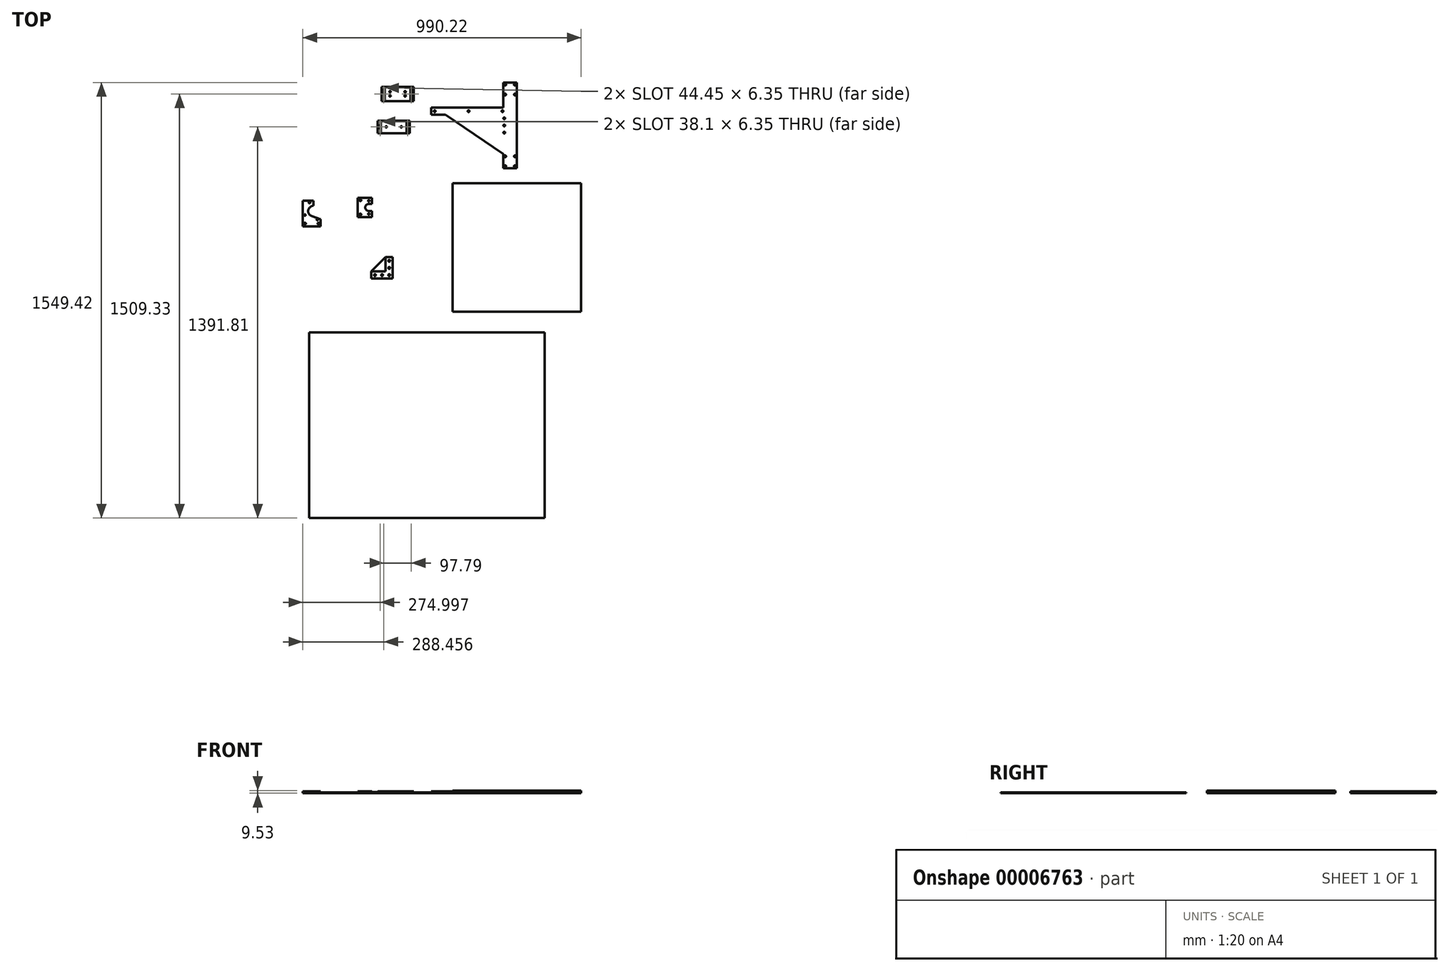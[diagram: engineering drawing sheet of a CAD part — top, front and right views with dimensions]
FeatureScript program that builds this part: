
annotation { "Feature Type Name" : "Feature", "Feature Type Description" : "" }
export const myFeature = defineFeature(function(context is Context, id is Id, definition is map)
    precondition{}
    {
        {
            var Q0;
            Q0=qCreatedBy(makeId("Top.planeOp"),FACE);
            var sketch = newSketch(context, id + "F0", { "sketchPlane" : qUnion([Q0])});
            skLineSegment(sketch, "E0.rect.bottom", {"start": v(228.6, 228.6) * mm, "end": v(-228.6, 228.6) * mm});
            skLineSegment(sketch, "E0.rect.top", {"start": v(228.6, -228.6) * mm, "end": v(-228.6, -228.6) * mm});
            skLineSegment(sketch, "E0.rect.left", {"start": v(228.6, 228.6) * mm, "end": v(228.6, -228.6) * mm});
            skLineSegment(sketch, "E0.rect.right", {"start": v(-228.6, 228.6) * mm, "end": v(-228.6, -228.6) * mm});
            skPoint(sketch, "E0.rect.middle", {"position": v(0, 0) * mm});
            skSolve(sketch);
        }
        {
            var Q0;
            Q0=makeQuery(id+"F0.imprint","IMPRINT",FACE,{"disambiguationData":[TD([[makeQuery(id+"F0.imprint","IMPRINT",EDGE,{"derivedFrom":sQuery(id+"F0.wireOp",EDGE,"E0.rect.bottom")}),1.0]])]});
            extrude(context, id + "F1", {"entities" : qUnion([Q0]), "depth" : 9.52 * mm});
        }
        {
            var Q0;
            Q0=qCreatedBy(makeId("Top.planeOp"),FACE);
            var sketch = newSketch(context, id + "F2", { "sketchPlane" : qUnion([Q0])});
            skLineSegment(sketch, "E1.rect.left", {"start": v(0, 281.9) * mm, "end": v(0, 586.7) * mm});
            skLineSegment(sketch, "E2", {"start": v(-47.75, 281.9) * mm, "end": v(0, 281.9) * mm});
            skLineSegment(sketch, "E3", {"start": v(-47.75, 586.7) * mm, "end": v(0, 586.7) * mm});
            skLineSegment(sketch, "E4", {"start": v(-304.8, 497.8) * mm, "end": v(-304.8, 472.4) * mm});
            skLineSegment(sketch, "E5", {"start": v(-47.75, 281.9) * mm, "end": v(-47.75, 332.7) * mm});
            skLineSegment(sketch, "E6", {"start": v(-47.75, 586.7) * mm, "end": v(-47.75, 497.8) * mm});
            skLineSegment(sketch, "E7", {"start": v(-304.8, 497.8) * mm, "end": v(-254, 497.8) * mm});
            skLineSegment(sketch, "E8", {"start": v(-254, 497.8) * mm, "end": v(-47.75, 497.8) * mm});
            skLineSegment(sketch, "E9", {"start": v(-304.8, 472.4) * mm, "end": v(-254, 472.4) * mm});
            skLineSegment(sketch, "E10", {"start": v(-254, 472.4) * mm, "end": v(-47.75, 332.7) * mm});
            skLineSegment(sketch, "E11", {"start": v(-304.8, 485.1) * mm, "end": v(0, 485.1) * mm, "construction": true});
            skLineSegment(sketch, "E12", {"start": v(-41.38, 586.7) * mm, "end": v(-41.38, 579.19) * mm, "construction": true});
            skLineSegment(sketch, "E13", {"start": v(-6.38, 586.7) * mm, "end": v(-6.38, 281.9) * mm, "construction": true});
            skLineSegment(sketch, "E14", {"start": v(-47.75, 579.19) * mm, "end": v(0, 579.19) * mm, "construction": true});
            skLineSegment(sketch, "E15", {"start": v(-47.75, 544.19) * mm, "end": v(0, 544.19) * mm, "construction": true});
            skLineSegment(sketch, "E16", {"start": v(-47.75, 324.43) * mm, "end": v(0, 324.43) * mm, "construction": true});
            skLineSegment(sketch, "E17", {"start": v(-47.75, 289.43) * mm, "end": v(-41.38, 289.43) * mm, "construction": true});
            skLineSegment(sketch, "E18", {"start": v(-41.38, 324.43) * mm, "end": v(-41.38, 289.43) * mm, "construction": true});
            skLineSegment(sketch, "E19", {"start": v(-41.38, 289.43) * mm, "end": v(-41.38, 281.9) * mm, "construction": true});
            skLineSegment(sketch, "E20", {"start": v(-41.38, 289.43) * mm, "end": v(-6.38, 289.43) * mm, "construction": true});
            skLineSegment(sketch, "E21", {"start": v(-6.38, 289.43) * mm, "end": v(0, 289.43) * mm, "construction": true});
            skLineSegment(sketch, "E22", {"start": v(-41.38, 579.19) * mm, "end": v(-41.38, 544.19) * mm, "construction": true});
            skLineSegment(sketch, "E23", {"start": v(-41.38, 544.19) * mm, "end": v(-41.38, 324.43) * mm, "construction": true});
            skPoint(sketch, "E24", {"position": v(-41.38, 306.93) * mm});
            skPoint(sketch, "E25", {"position": v(-41.38, 561.69) * mm});
            skCircle(sketch, "E26", {"center": v(-41.38, 324.43) * mm, "radius": 3.2 * mm});
            skCircle(sketch, "E27", {"center": v(-6.38, 324.43) * mm, "radius": 3.2 * mm});
            skCircle(sketch, "E28", {"center": v(-41.38, 289.43) * mm, "radius": 3.2 * mm});
            skCircle(sketch, "E29", {"center": v(-6.38, 289.43) * mm, "radius": 3.2 * mm});
            skCircle(sketch, "E30", {"center": v(-41.38, 579.19) * mm, "radius": 3.2 * mm});
            skCircle(sketch, "E31", {"center": v(-6.38, 579.19) * mm, "radius": 3.2 * mm});
            skCircle(sketch, "E32", {"center": v(-41.38, 544.19) * mm, "radius": 3.2 * mm});
            skCircle(sketch, "E33", {"center": v(-6.38, 544.19) * mm, "radius": 3.2 * mm});
            skCircle(sketch, "E34", {"center": v(-171.45, 485.1) * mm, "radius": 3.17 * mm});
            skCircle(sketch, "E35", {"center": v(-50.8, 485.1) * mm, "radius": 3.17 * mm});
            skCircle(sketch, "E36", {"center": v(-292.1, 485.1) * mm, "radius": 3.17 * mm});
            skCircle(sketch, "E37", {"center": v(-69.85, 459.7) * mm, "radius": 2.55 * mm, "construction": true});
            skCircle(sketch, "E38", {"center": v(-69.85, 434.3) * mm, "radius": 2.55 * mm, "construction": true});
            skCircle(sketch, "E39", {"center": v(-95.25, 459.7) * mm, "radius": 2.55 * mm, "construction": true});
            skCircle(sketch, "E40", {"center": v(-95.25, 434.3) * mm, "radius": 2.55 * mm, "construction": true});
            skLineSegment(sketch, "E41", {"start": v(-44.45, 608.23) * mm, "end": v(-44.45, 265.2) * mm, "construction": true});
            skCircle(sketch, "E42", {"center": v(-44.45, 459.7) * mm, "radius": 3.17 * mm});
            skCircle(sketch, "E43", {"center": v(-44.45, 434.3) * mm, "radius": 3.17 * mm});
            skCircle(sketch, "E44", {"center": v(-44.45, 408.9) * mm, "radius": 3.18 * mm});
            skSolve(sketch);
        }
        {
            var Q0;
            Q0=makeQuery(id+"F2.imprint","IMPRINT",FACE,{"disambiguationData":[TD([[makeQuery(id+"F2.imprint","IMPRINT",EDGE,{"derivedFrom":sQuery(id+"F2.wireOp",EDGE,"E1.rect.left")}),1.0]])]});
            extrude(context, id + "F3", {"entities" : qUnion([Q0]), "depth" : 6.35 * mm});
        }
        {
            var Q0;
            Q0=qCreatedBy(makeId("Top.planeOp"),FACE);
            var sketch = newSketch(context, id + "F4", { "sketchPlane" : qUnion([Q0])});
            skLineSegment(sketch, "E45", {"start": v(-517.53, -110.74) * mm, "end": v(-441.33, -110.74) * mm});
            skLineSegment(sketch, "E46", {"start": v(-441.33, -110.74) * mm, "end": v(-441.33, -34.54) * mm});
            skLineSegment(sketch, "E47", {"start": v(-441.33, -34.54) * mm, "end": v(-466.73, -34.54) * mm});
            skLineSegment(sketch, "E48", {"start": v(-466.73, -34.54) * mm, "end": v(-466.73, -85.34) * mm});
            skLineSegment(sketch, "E49", {"start": v(-466.73, -85.34) * mm, "end": v(-517.53, -85.34) * mm});
            skLineSegment(sketch, "E50", {"start": v(-517.53, -85.34) * mm, "end": v(-517.53, -110.74) * mm});
            skCircle(sketch, "E51", {"center": v(-454.03, -98.04) * mm, "radius": 3.26 * mm});
            skCircle(sketch, "E52.1.0.0", {"center": v(-454.03, -72.64) * mm, "radius": 3.26 * mm});
            skCircle(sketch, "E52.2.0.0", {"center": v(-454.03, -47.24) * mm, "radius": 3.26 * mm});
            skLineSegment(sketch, "E52.direction1", {"start": v(-454.03, -98.04) * mm, "end": v(-454.03, -72.64) * mm, "construction": true});
            skCircle(sketch, "E53.1.0.0", {"center": v(-479.43, -98.04) * mm, "radius": 3.26 * mm});
            skCircle(sketch, "E53.2.0.0", {"center": v(-504.83, -98.04) * mm, "radius": 3.26 * mm});
            skLineSegment(sketch, "E53.direction1", {"start": v(-454.03, -98.04) * mm, "end": v(-479.43, -98.04) * mm, "construction": true});
            skLineSegment(sketch, "E54", {"start": v(-517.53, -85.34) * mm, "end": v(-466.73, -34.54) * mm});
            skSolve(sketch);
        }
        {
            var Q0;
            Q0=makeQuery(id+"F4.imprint","IMPRINT",FACE,{"disambiguationData":[TD([[makeQuery(id+"F4.imprint","IMPRINT",EDGE,{"derivedFrom":sQuery(id+"F4.wireOp",EDGE,"E45")}),1.0]])]});
            extrude(context, id + "F5", {"entities" : qUnion([Q0]), "depth" : 4.78 * mm});
        }
        {
            var Q0;
            Q0=makeQuery(id+"F4.imprint","IMPRINT",FACE,{"disambiguationData":[TD([[makeQuery(id+"F4.imprint","IMPRINT",EDGE,{"derivedFrom":sQuery(id+"F4.wireOp",EDGE,"E48")}),-1.0]])]});
            var Q1;
            Q1=makeQuery(id+"F4.imprint","IMPRINT",FACE,{"disambiguationData":[TD([[makeQuery(id+"F4.imprint","IMPRINT",EDGE,{"derivedFrom":sQuery(id+"F4.wireOp",EDGE,"E45")}),1.0]])]});
            extrude(context, id + "F6", {"entities" : qUnion([Q0, Q1]), "depth" : 4.78 * mm});
        }
        {
            var Q0;
            Q0=qCreatedBy(makeId("Top.planeOp"),FACE);
            var sketch = newSketch(context, id + "F7", { "sketchPlane" : qUnion([Q0])});
            skLineSegment(sketch, "E55.bottom", {"start": v(-566.8, 176.8) * mm, "end": v(-526.52, 176.8) * mm});
            skLineSegment(sketch, "E55.top", {"start": v(-566.8, 108.21) * mm, "end": v(-526.52, 108.21) * mm});
            skLineSegment(sketch, "E55.left", {"start": v(-566.8, 176.8) * mm, "end": v(-566.8, 108.21) * mm});
            skLineSegment(sketch, "E55.right", {"start": v(-526.52, 176.8) * mm, "end": v(-526.52, 155.2) * mm, "construction": true});
            skArc(sketch, "E56", {"start": v(-526.52, 155.2) * mm, "mid": v(-539.22, 142.5) * mm, "end": v(-526.52, 129.8) * mm});
            skLineSegment(sketch, "E57.trimOffspring", {"start": v(-526.52, 129.8) * mm, "end": v(-526.52, 108.21) * mm, "construction": true});
            skLineSegment(sketch, "E58", {"start": v(-526.52, 108.21) * mm, "end": v(-516, 108.21) * mm});
            skLineSegment(sketch, "E59", {"start": v(-516, 108.21) * mm, "end": v(-516, 129.8) * mm});
            skLineSegment(sketch, "E60", {"start": v(-516, 129.8) * mm, "end": v(-526.52, 129.8) * mm});
            skLineSegment(sketch, "E61", {"start": v(-526.52, 155.2) * mm, "end": v(-516, 155.2) * mm});
            skLineSegment(sketch, "E62", {"start": v(-516, 155.2) * mm, "end": v(-516, 176.8) * mm});
            skLineSegment(sketch, "E63", {"start": v(-516, 176.8) * mm, "end": v(-526.52, 176.8) * mm});
            skCircle(sketch, "E64", {"center": v(-526.52, 166) * mm, "radius": 2.55 * mm});
            skCircle(sketch, "E65", {"center": v(-526.52, 119) * mm, "radius": 2.55 * mm});
            skCircle(sketch, "E66", {"center": v(-556.64, 167.9) * mm, "radius": 3.18 * mm});
            skCircle(sketch, "E67", {"center": v(-556.64, 117.1) * mm, "radius": 3.18 * mm});
            skSolve(sketch);
        }
        {
            var Q0;
            Q0=makeQuery(id+"F7.imprint","IMPRINT",FACE,{"disambiguationData":[TD([[makeQuery(id+"F7.imprint","IMPRINT",EDGE,{"derivedFrom":sQuery(id+"F7.wireOp",EDGE,"E55.bottom")}),-1.0]])]});
            extrude(context, id + "F8", {"entities" : qUnion([Q0]), "depth" : 6.35 * mm});
        }
        {
            var Q0;
            Q0=qCreatedBy(makeId("Top.planeOp"),FACE);
            var sketch = newSketch(context, id + "F9", { "sketchPlane" : qUnion([Q0])});
            skLineSegment(sketch, "E68.rect.bottom", {"start": v(99.07, -962.71) * mm, "end": v(-739.13, -962.71) * mm});
            skLineSegment(sketch, "E68.rect.top", {"start": v(99.07, -302.31) * mm, "end": v(-739.13, -302.31) * mm});
            skLineSegment(sketch, "E68.rect.left", {"start": v(99.07, -962.71) * mm, "end": v(99.07, -302.31) * mm});
            skLineSegment(sketch, "E68.rect.right", {"start": v(-739.13, -962.71) * mm, "end": v(-739.13, -302.31) * mm});
            skPoint(sketch, "E68.rect.middle", {"position": v(-320.03, -632.51) * mm});
            skSolve(sketch);
        }
        {
            var Q0;
            Q0=makeQuery(id+"F9.imprint","IMPRINT",FACE,{"disambiguationData":[TD([[makeQuery(id+"F9.imprint","IMPRINT",EDGE,{"derivedFrom":sQuery(id+"F9.wireOp",EDGE,"E68.rect.bottom")}),-1.0]])]});
            extrude(context, id + "F10", {"entities" : qUnion([Q0]), "depth" : 3.17 * mm});
        }
        {
            var Q0;
            Q0=makeQuery(id+"F1.opExtrude","CAP_FACE",FACE,{"disambiguationData":[OSD([sQuery(id+"F0.wireOp",EDGE,"E0.rect.bottom"),sQuery(id+"F0.wireOp",EDGE,"E0.rect.top"),sQuery(id+"F0.wireOp",EDGE,"E0.rect.left"),sQuery(id+"F0.wireOp",EDGE,"E0.rect.right")])],"isStart":true});
            var sketch = newSketch(context, id + "F11", { "sketchPlane" : qUnion([Q0])});
            skLineSegment(sketch, "E69", {"start": v(0, 177.8) * mm, "end": v(152.4, 177.8) * mm, "construction": true});
            skLineSegment(sketch, "E70", {"start": v(76.2, 59.27) * mm, "end": v(-76.2, 59.27) * mm, "construction": true});
            skLineSegment(sketch, "E71", {"start": v(-152.4, -59.27) * mm, "end": v(152.4, -59.27) * mm, "construction": true});
            skLineSegment(sketch, "E72", {"start": v(76.2, -177.8) * mm, "end": v(-76.2, -177.8) * mm, "construction": true});
            skLineSegment(sketch, "E73", {"start": v(76.2, -177.8) * mm, "end": v(76.2, -59.27) * mm, "construction": true});
            skLineSegment(sketch, "E74", {"start": v(76.2, -59.27) * mm, "end": v(76.2, 59.27) * mm, "construction": true});
            skLineSegment(sketch, "E75", {"start": v(76.2, 59.27) * mm, "end": v(76.2, 177.8) * mm, "construction": true});
            skPoint(sketch, "E76", {"position": v(0, 177.8) * mm});
            skPoint(sketch, "E77", {"position": v(0, -59.27) * mm});
            skLineSegment(sketch, "E78", {"start": v(76.2, 177.8) * mm, "end": v(76.2, 228.6) * mm, "construction": true});
            skLineSegment(sketch, "E79", {"start": v(76.2, -177.8) * mm, "end": v(76.2, -228.6) * mm, "construction": true});
            skLineSegment(sketch, "E80", {"start": v(-152.4, 177.8) * mm, "end": v(-228.6, 177.8) * mm, "construction": true});
            skLineSegment(sketch, "E81", {"start": v(-76.2, 59.27) * mm, "end": v(-228.6, 59.27) * mm, "construction": true});
            skLineSegment(sketch, "E82", {"start": v(152.4, 177.8) * mm, "end": v(228.6, 177.8) * mm, "construction": true});
            skLineSegment(sketch, "E83", {"start": v(76.2, 59.27) * mm, "end": v(228.6, 59.27) * mm, "construction": true});
            skLineSegment(sketch, "E84", {"start": v(-152.4, 177.8) * mm, "end": v(0, 177.8) * mm, "construction": true});
            skSolve(sketch);
        }
        {
            var Q0;
            Q0=qCreatedBy(makeId("Top.planeOp"),FACE);
            var sketch = newSketch(context, id + "F12", { "sketchPlane" : qUnion([Q0])});
            skLineSegment(sketch, "E85.bottom", {"start": v(-481.42, 572.02) * mm, "end": v(-367.12, 572.02) * mm});
            skLineSegment(sketch, "E85.top", {"start": v(-481.42, 521.22) * mm, "end": v(-367.12, 521.22) * mm});
            skLineSegment(sketch, "E85.left", {"start": v(-481.42, 572.02) * mm, "end": v(-481.42, 521.22) * mm});
            skLineSegment(sketch, "E85.right", {"start": v(-367.12, 572.02) * mm, "end": v(-367.12, 521.22) * mm});
            skLineSegment(sketch, "E86.bottom", {"start": v(-494.88, 451.32) * mm, "end": v(-380.58, 451.32) * mm});
            skLineSegment(sketch, "E86.top", {"start": v(-494.88, 406.87) * mm, "end": v(-380.58, 406.87) * mm});
            skLineSegment(sketch, "E86.left", {"start": v(-494.88, 451.32) * mm, "end": v(-494.88, 406.87) * mm});
            skLineSegment(sketch, "E86.right", {"start": v(-380.58, 451.32) * mm, "end": v(-380.58, 406.87) * mm});
            skLineSegment(sketch, "E87", {"start": v(-494.88, 429.1) * mm, "end": v(-464.73, 429.1) * mm, "construction": true});
            skLineSegment(sketch, "E88", {"start": v(-481.42, 554.24) * mm, "end": v(-451.27, 554.24) * mm, "construction": true});
            skLineSegment(sketch, "E89", {"start": v(-481.42, 539.26) * mm, "end": v(-367.12, 539.26) * mm, "construction": true});
            skCircle(sketch, "E90", {"center": v(-464.73, 429.1) * mm, "radius": 2.55 * mm});
            skCircle(sketch, "E91", {"center": v(-410.73, 429.1) * mm, "radius": 2.55 * mm});
            skCircle(sketch, "E92", {"center": v(-451.27, 554.24) * mm, "radius": 2.55 * mm});
            skCircle(sketch, "E93", {"center": v(-397.27, 554.24) * mm, "radius": 2.55 * mm});
            skCircle(sketch, "E94", {"center": v(-451.27, 539.26) * mm, "radius": 2.55 * mm});
            skCircle(sketch, "E95", {"center": v(-397.27, 539.26) * mm, "radius": 2.55 * mm});
            skLineSegment(sketch, "E96", {"start": v(-476.34, 565.67) * mm, "end": v(-476.34, 527.57) * mm});
            skLineSegment(sketch, "E97", {"start": v(-469.99, 565.67) * mm, "end": v(-469.99, 527.57) * mm});
            skLineSegment(sketch, "E98", {"start": v(-424.27, 572.02) * mm, "end": v(-424.27, 521.22) * mm, "construction": true});
            skArc(sketch, "E99", {"start": v(-469.99, 527.57) * mm, "mid": v(-473.16, 524.4) * mm, "end": v(-476.34, 527.57) * mm});
            skArc(sketch, "E100", {"start": v(-476.34, 565.67) * mm, "mid": v(-473.16, 568.85) * mm, "end": v(-469.99, 565.67) * mm});
            skLineSegment(sketch, "E101.MirrorCS", {"start": v(-372.2, 565.67) * mm, "end": v(-372.2, 527.57) * mm});
            skLineSegment(sketch, "E102.MirrorCS", {"start": v(-378.55, 565.67) * mm, "end": v(-378.55, 527.57) * mm});
            skArc(sketch, "E103.MirrorCS", {"start": v(-372.2, 565.67) * mm, "mid": v(-375.37, 568.85) * mm, "end": v(-378.55, 565.67) * mm});
            skArc(sketch, "E104.MirrorCS", {"start": v(-378.55, 527.57) * mm, "mid": v(-375.37, 524.4) * mm, "end": v(-372.2, 527.57) * mm});
            skLineSegment(sketch, "E105", {"start": v(-451.27, 554.24) * mm, "end": v(-397.27, 554.24) * mm, "construction": true});
            skLineSegment(sketch, "E106", {"start": v(-397.27, 554.24) * mm, "end": v(-367.12, 554.24) * mm, "construction": true});
            skLineSegment(sketch, "E107", {"start": v(-464.73, 429.1) * mm, "end": v(-410.73, 429.1) * mm, "construction": true});
            skLineSegment(sketch, "E108", {"start": v(-410.73, 429.1) * mm, "end": v(-380.58, 429.1) * mm, "construction": true});
            skLineSegment(sketch, "E109", {"start": v(-486.62, 444.97) * mm, "end": v(-486.62, 413.22) * mm, "construction": true});
            skLineSegment(sketch, "E110", {"start": v(-437.73, 429.1) * mm, "end": v(-437.73, 437.33) * mm, "construction": true});
            skArc(sketch, "E111", {"start": v(-483.45, 444.97) * mm, "mid": v(-486.62, 448.15) * mm, "end": v(-489.8, 444.97) * mm});
            skArc(sketch, "E112", {"start": v(-483.45, 413.22) * mm, "mid": v(-486.62, 410.05) * mm, "end": v(-489.8, 413.22) * mm});
            skLineSegment(sketch, "E113", {"start": v(-483.45, 444.97) * mm, "end": v(-483.45, 413.22) * mm});
            skLineSegment(sketch, "E114", {"start": v(-489.8, 444.97) * mm, "end": v(-489.8, 413.22) * mm});
            skLineSegment(sketch, "E115.MirrorCS", {"start": v(-392, 444.97) * mm, "end": v(-392, 413.22) * mm});
            skArc(sketch, "E116.MirrorCS", {"start": v(-392, 444.97) * mm, "mid": v(-388.83, 448.15) * mm, "end": v(-385.66, 444.97) * mm});
            skLineSegment(sketch, "E117.MirrorCS", {"start": v(-385.66, 444.97) * mm, "end": v(-385.66, 413.22) * mm});
            skArc(sketch, "E118.MirrorCS", {"start": v(-392, 413.22) * mm, "mid": v(-388.83, 410.05) * mm, "end": v(-385.66, 413.22) * mm});
            skLineSegment(sketch, "E119", {"start": v(-486.62, 444.97) * mm, "end": v(-486.62, 451.32) * mm, "construction": true});
            skPoint(sketch, "E119.endSnap0", {"position": v(-486.62, 448.15) * mm});
            skLineSegment(sketch, "E120", {"start": v(-486.62, 413.22) * mm, "end": v(-486.62, 406.87) * mm, "construction": true});
            skLineSegment(sketch, "E121", {"start": v(-473.16, 565.67) * mm, "end": v(-473.16, 572.02) * mm, "construction": true});
            skLineSegment(sketch, "E122", {"start": v(-473.16, 565.67) * mm, "end": v(-473.16, 527.57) * mm, "construction": true});
            skLineSegment(sketch, "E123", {"start": v(-473.16, 527.57) * mm, "end": v(-473.16, 521.22) * mm, "construction": true});
            skSolve(sketch);
        }
        {
            var Q0;
            Q0=makeQuery(id+"F12.imprint","IMPRINT",FACE,{"disambiguationData":[TD([[makeQuery(id+"F12.imprint","IMPRINT",EDGE,{"derivedFrom":sQuery(id+"F12.wireOp",EDGE,"E85.bottom")}),-1.0]])]});
            var Q1;
            Q1=makeQuery(id+"F12.imprint","IMPRINT",FACE,{"disambiguationData":[TD([[makeQuery(id+"F12.imprint","IMPRINT",EDGE,{"derivedFrom":sQuery(id+"F12.wireOp",EDGE,"E86.bottom")}),-1.0]])]});
            extrude(context, id + "F13", {"entities" : qUnion([Q0, Q1]), "depth" : 6.35 * mm});
        }
        {
            var Q0;
            Q0=qCreatedBy(makeId("Top.planeOp"),FACE);
            var sketch = newSketch(context, id + "F14", { "sketchPlane" : qUnion([Q0])});
            skLineSegment(sketch, "E124.rect.bottom", {"start": v(-698.12, 74.9) * mm, "end": v(-761.62, 74.9) * mm});
            skLineSegment(sketch, "E124.rect.top", {"start": v(-723.52, 166.35) * mm, "end": v(-761.62, 166.35) * mm});
            skLineSegment(sketch, "E124.rect.left", {"start": v(-698.12, 74.9) * mm, "end": v(-698.12, 99.87) * mm});
            skLineSegment(sketch, "E124.rect.right", {"start": v(-761.62, 74.9) * mm, "end": v(-761.62, 166.35) * mm});
            skPoint(sketch, "E124.rect.middle", {"position": v(-729.87, 120.63) * mm});
            skCircle(sketch, "E125", {"center": v(-754, 85.07) * mm, "radius": 3.18 * mm});
            skCircle(sketch, "E126", {"center": v(-705.74, 85.07) * mm, "radius": 3.18 * mm});
            skArc(sketch, "E127", {"start": v(-723.52, 148.44) * mm, "mid": v(-742.28, 132.7) * mm, "end": v(-730.03, 111.48) * mm});
            skLineSegment(sketch, "E128", {"start": v(-730.03, 111.48) * mm, "end": v(-698.12, 99.87) * mm});
            skPoint(sketch, "E129.orphan", {"position": v(-698.12, 166.35) * mm});
            skLineSegment(sketch, "E130", {"start": v(-723.52, 148.44) * mm, "end": v(-723.52, 148.44) * mm});
            skLineSegment(sketch, "E131", {"start": v(-723.52, 148.44) * mm, "end": v(-723.52, 166.35) * mm});
            skLineSegment(sketch, "E132", {"start": v(-723.52, 166.35) * mm, "end": v(-723.52, 166.35) * mm});
            skCircle(sketch, "E133", {"center": v(-737.6, 159.57) * mm, "radius": 2.54 * mm});
            skCircle(sketch, "E134", {"center": v(-753.7, 115.31) * mm, "radius": 2.54 * mm});
            skCircle(sketch, "E135", {"center": v(-709.44, 99.2) * mm, "radius": 2.54 * mm});
            skCircle(sketch, "E136", {"center": v(-693.33, 143.46) * mm, "radius": 2.54 * mm});
            skLineSegment(sketch, "E137", {"start": v(-737.6, 159.57) * mm, "end": v(-753.7, 115.31) * mm, "construction": true});
            skLineSegment(sketch, "E138", {"start": v(-753.7, 115.31) * mm, "end": v(-709.44, 99.2) * mm, "construction": true});
            skLineSegment(sketch, "E139", {"start": v(-693.33, 143.46) * mm, "end": v(-709.44, 99.2) * mm, "construction": true});
            skLineSegment(sketch, "E140", {"start": v(-693.33, 143.46) * mm, "end": v(-737.6, 159.57) * mm, "construction": true});
            skLineSegment(sketch, "E141", {"start": v(-737.6, 159.57) * mm, "end": v(-709.44, 99.2) * mm, "construction": true});
            skSolve(sketch);
        }
        {
            var Q0;
            Q0=makeQuery(id+"F14.imprint","IMPRINT",FACE,{"disambiguationData":[TD([[makeQuery(id+"F14.imprint","IMPRINT",EDGE,{"derivedFrom":sQuery(id+"F14.wireOp",EDGE,"E124.rect.bottom")}),-1.0]])]});
            extrude(context, id + "F15", {"entities" : qUnion([Q0]), "depth" : 6.35 * mm});
        }
    });
